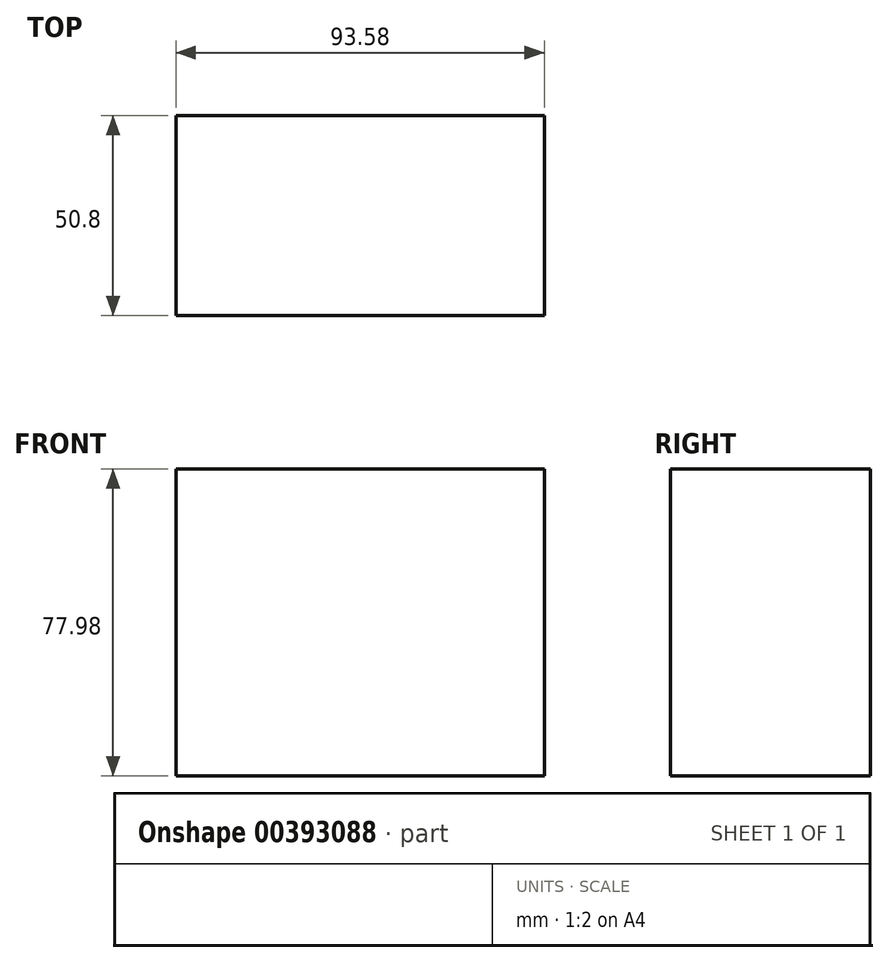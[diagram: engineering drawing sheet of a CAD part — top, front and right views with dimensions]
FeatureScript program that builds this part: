
annotation { "Feature Type Name" : "Feature", "Feature Type Description" : "" }
export const myFeature = defineFeature(function(context is Context, id is Id, definition is map)
    precondition{}
    {
        {
            var Q0;
            Q0=qCreatedBy(makeId("Front.planeOp"),FACE);
            var sketch = newSketch(context, id + "F0", { "sketchPlane" : qUnion([Q0])});
            skLineSegment(sketch, "E0.bottom", {"start": v(46.8, 39) * mm, "end": v(-46.8, 39) * mm});
            skLineSegment(sketch, "E0.top", {"start": v(46.8, -39) * mm, "end": v(-46.8, -39) * mm});
            skLineSegment(sketch, "E0.left", {"start": v(46.8, 39) * mm, "end": v(46.8, -39) * mm});
            skLineSegment(sketch, "E0.right", {"start": v(-46.8, 39) * mm, "end": v(-46.8, -39) * mm});
            skPoint(sketch, "E0.middle", {"position": v(0, 0) * mm});
            skSolve(sketch);
        }
        {
            var Q0;
            Q0 = qSketchRegion(id + "F0", true);
            extrude(context, id + "F1", {"entities" : qUnion([Q0]), "depth" : 50.8 * mm});
        }
    });
